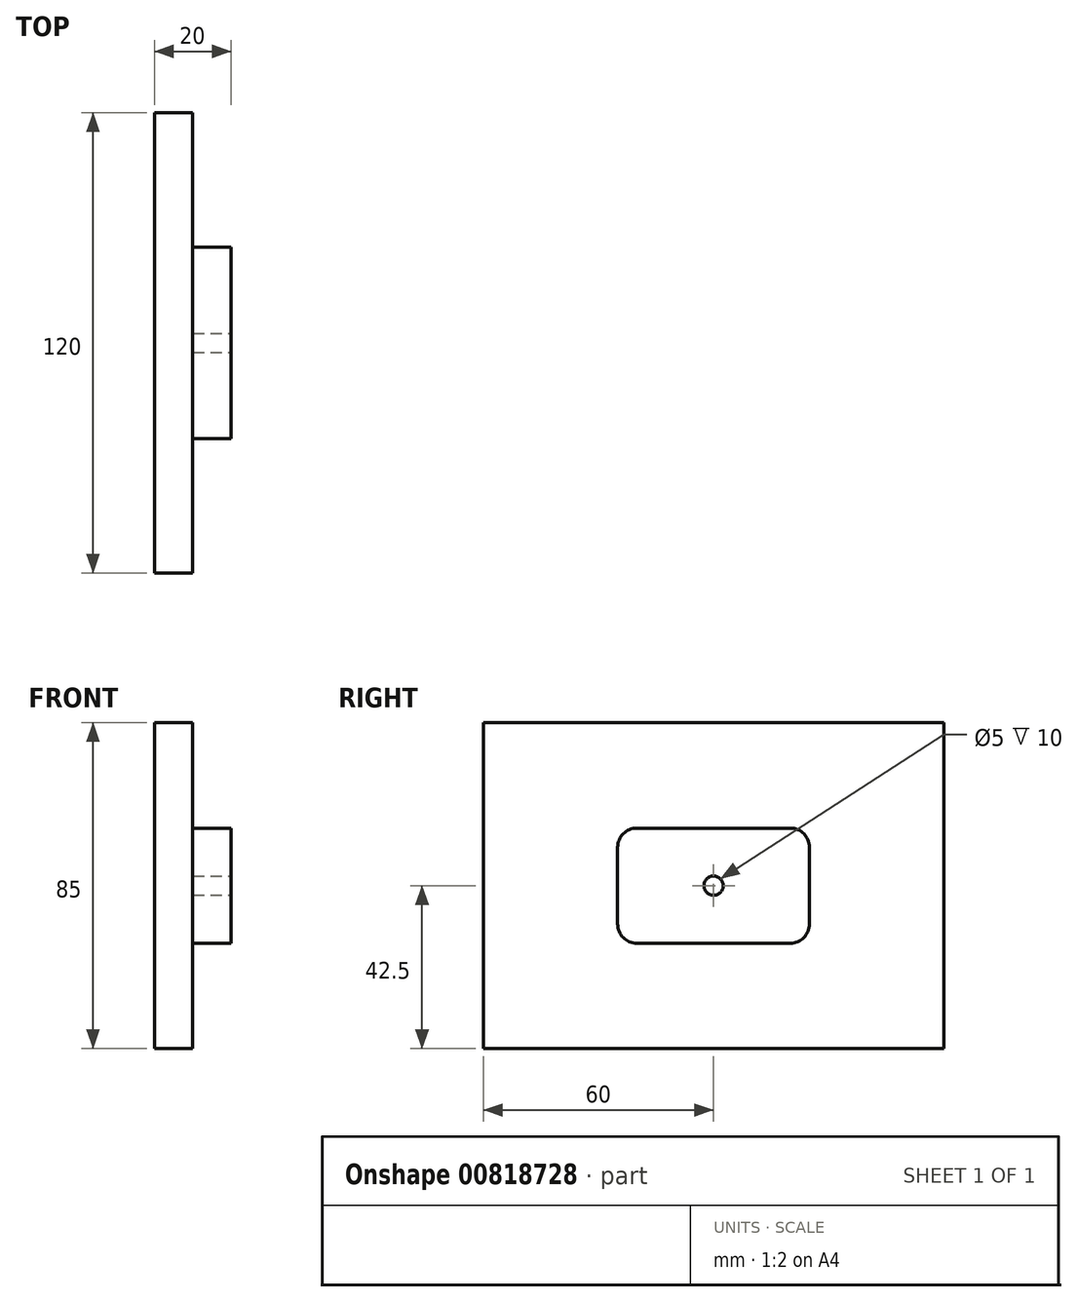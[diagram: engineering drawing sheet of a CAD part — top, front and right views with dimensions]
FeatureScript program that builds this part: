
annotation { "Feature Type Name" : "Feature", "Feature Type Description" : "" }
export const myFeature = defineFeature(function(context is Context, id is Id, definition is map)
    precondition{}
    {
        {
            var Q0;
            Q0=qCreatedBy(makeId("Right.planeOp"),FACE);
            var sketch = newSketch(context, id + "F0", { "sketchPlane" : qUnion([Q0])});
            skLineSegment(sketch, "E0.bottom", {"start": v(60, -42.5) * mm, "end": v(-60, -42.5) * mm});
            skLineSegment(sketch, "E0.top", {"start": v(60, 42.5) * mm, "end": v(-60, 42.5) * mm});
            skLineSegment(sketch, "E0.left", {"start": v(60, -42.5) * mm, "end": v(60, 42.5) * mm});
            skLineSegment(sketch, "E0.right", {"start": v(-60, -42.5) * mm, "end": v(-60, 42.5) * mm});
            skPoint(sketch, "E0.middle", {"position": v(0, 0) * mm});
            skLineSegment(sketch, "E1.bottom", {"start": v(25, 15) * mm, "end": v(-25, 15) * mm});
            skLineSegment(sketch, "E1.top", {"start": v(25, -15) * mm, "end": v(-25, -15) * mm});
            skLineSegment(sketch, "E1.left", {"start": v(25, 15) * mm, "end": v(25, -15) * mm});
            skLineSegment(sketch, "E1.right", {"start": v(-25, 15) * mm, "end": v(-25, -15) * mm});
            skSolve(sketch);
        }
        {
            var Q0;
            Q0=makeQuery(id+"F0.imprint","IMPRINT",FACE,{"disambiguationData":[TD([[makeQuery(id+"F0.imprint","IMPRINT",EDGE,{"derivedFrom":sQuery(id+"F0.wireOp",EDGE,"E1.bottom")}),1.0]])]});
            var Q1;
            Q1=makeQuery(id+"F0.imprint","IMPRINT",FACE,{"disambiguationData":[TD([[makeQuery(id+"F0.imprint","IMPRINT",EDGE,{"derivedFrom":sQuery(id+"F0.wireOp",EDGE,"E0.bottom")}),-1.0]])]});
            extrude(context, id + "F1", {"entities" : qUnion([Q0, Q1]), "depth" : 10 * mm, "offsetDistance" : 25 * mm});
        }
        {
            var Q0;
            Q0=makeQuery(id+"F0.imprint","IMPRINT",FACE,{"disambiguationData":[TD([[makeQuery(id+"F0.imprint","IMPRINT",EDGE,{"derivedFrom":sQuery(id+"F0.wireOp",EDGE,"E1.bottom")}),1.0]])]});
            extrude(context, id + "F2", {"entities" : qUnion([Q0]), "operationType" : NewBodyOperationType.ADD, "depth" : 20 * mm, "offsetDistance" : 25 * mm});
        }
        {
            var Q0;
            Q0=makeQuery(id+"F2.opExtrude","CAP_FACE",FACE,{"disambiguationData":[OSD([sQuery(id+"F0.wireOp",EDGE,"E1.bottom"),sQuery(id+"F0.wireOp",EDGE,"E1.top"),sQuery(id+"F0.wireOp",EDGE,"E1.left"),sQuery(id+"F0.wireOp",EDGE,"E1.right")])],"isStart":false});
            var sketch = newSketch(context, id + "F3", { "sketchPlane" : qUnion([Q0])});
            skCircle(sketch, "E2", {"center": v(0, 0) * mm, "radius": 2.5 * mm});
            skSolve(sketch);
        }
        {
            var Q0;
            Q0=makeQuery(id+"F3.imprint","IMPRINT",FACE,{"disambiguationData":[TD([[makeQuery(id+"F3.imprint","IMPRINT",EDGE,{"derivedFrom":sQuery(id+"F3.wireOp",EDGE,"E2")}),1.0]])]});
            extrude(context, id + "F4", {"entities" : qUnion([Q0]), "operationType" : NewBodyOperationType.REMOVE, "oppositeDirection" : true, "depth" : 10 * mm, "offsetDistance" : 25 * mm});
        }
        {
            var Q0;
            Q0=makeQuery(id+"F2.opExtrude","SWEPT_EDGE",EDGE,{"disambiguationData":[OSD([sQuery(id+"F0.wireOp",EDGE,"E1.bottom"),sQuery(id+"F0.wireOp",EDGE,"E1.right")])]});
            var Q1;
            Q1=makeQuery(id+"F2.opExtrude","SWEPT_EDGE",EDGE,{"disambiguationData":[OSD([sQuery(id+"F0.wireOp",EDGE,"E1.bottom"),sQuery(id+"F0.wireOp",EDGE,"E1.left")])]});
            var Q2;
            Q2=makeQuery(id+"F2.opExtrude","SWEPT_EDGE",EDGE,{"disambiguationData":[OSD([sQuery(id+"F0.wireOp",EDGE,"E1.top"),sQuery(id+"F0.wireOp",EDGE,"E1.right")])]});
            var Q3;
            Q3=makeQuery(id+"F2.opExtrude","SWEPT_EDGE",EDGE,{"disambiguationData":[OSD([sQuery(id+"F0.wireOp",EDGE,"E1.top"),sQuery(id+"F0.wireOp",EDGE,"E1.left")])]});
            fillet(context, id + "F5", {"entities" : qUnion([Q0, Q1, Q2, Q3]), "radius" : 5 * mm, "tangentPropagation" : true, "allowEdgeOverflow" : false});
        }
    });
